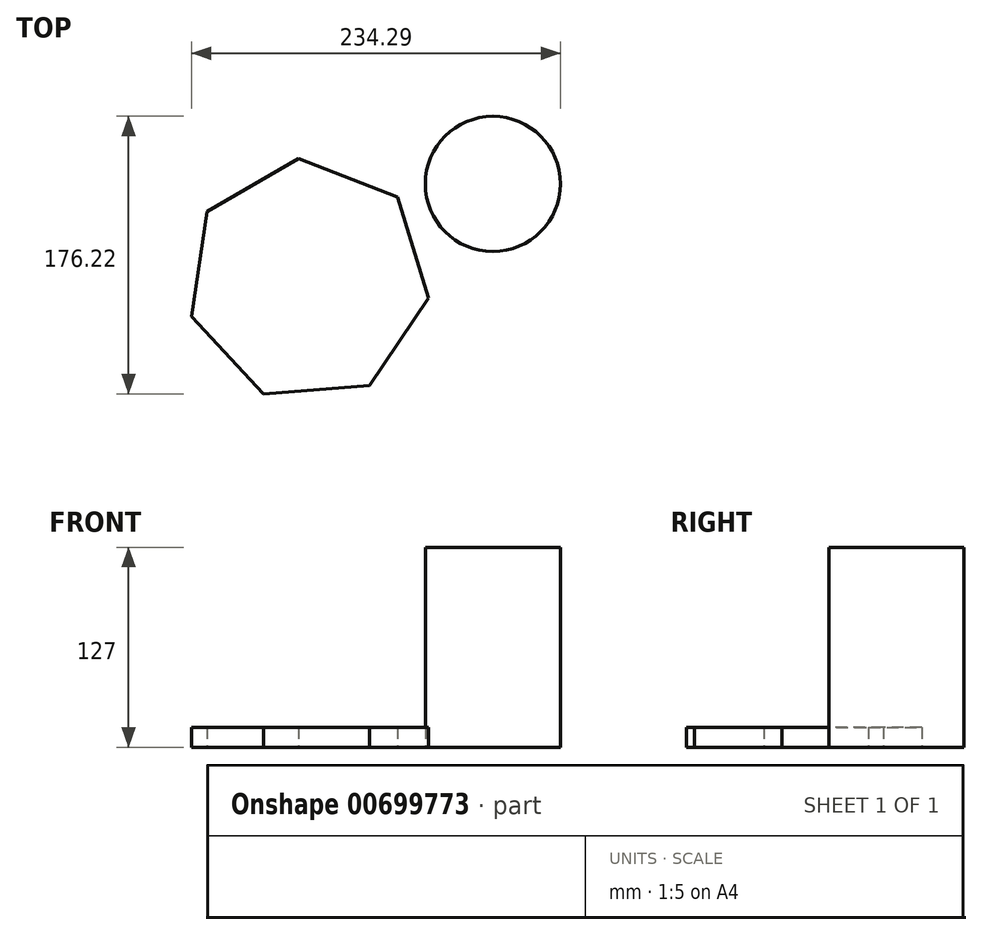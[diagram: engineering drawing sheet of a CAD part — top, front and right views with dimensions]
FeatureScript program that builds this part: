
annotation { "Feature Type Name" : "Feature", "Feature Type Description" : "" }
export const myFeature = defineFeature(function(context is Context, id is Id, definition is map)
    precondition{}
    {
        {
            var Q0;
            Q0=qCreatedBy(makeId("Top.planeOp"),FACE);
            var sketch = newSketch(context, id + "F0", { "sketchPlane" : qUnion([Q0])});
            skCircle(sketch, "E0.cCircle", {"center": v(-129.2, -13.24) * mm, "radius": 69.81 * mm, "construction": true});
            skLineSegment(sketch, "E0.0", {"start": v(-72.52, 39.59) * mm, "end": v(-52.56, -24.62) * mm});
            skLineSegment(sketch, "E0.1", {"start": v(-52.56, -24.62) * mm, "end": v(-90.31, -80.26) * mm});
            skLineSegment(sketch, "E0.2", {"start": v(-90.31, -80.26) * mm, "end": v(-157.35, -85.43) * mm});
            skLineSegment(sketch, "E0.3", {"start": v(-157.35, -85.43) * mm, "end": v(-203.2, -36.24) * mm});
            skLineSegment(sketch, "E0.4", {"start": v(-203.2, -36.24) * mm, "end": v(-193.32, 30.27) * mm});
            skLineSegment(sketch, "E0.5", {"start": v(-193.32, 30.27) * mm, "end": v(-135.16, 64.02) * mm});
            skLineSegment(sketch, "E0.6", {"start": v(-135.16, 64.02) * mm, "end": v(-72.52, 39.59) * mm});
            skPoint(sketch, "E0.0.midPoint", {"position": v(-62.54, 7.48) * mm});
            skSolve(sketch);
        }
        {
            var Q0;
            Q0=makeQuery(id+"F0.imprint","IMPRINT",FACE,{"disambiguationData":[TD([[makeQuery(id+"F0.imprint","IMPRINT",EDGE,{"derivedFrom":sQuery(id+"F0.wireOp",EDGE,"E0.0")}),-1.0]])]});
            var sketch = newSketch(context, id + "F1", { "sketchPlane" : qUnion([Q0])});
            skSolve(sketch);
        }
        {
            var Q0;
            Q0 = qSketchRegion(id + "F1", true);
            var Q1;
            Q1 = qSketchRegion(id + "F0", true);
            extrude(context, id + "F2", {"entities" : qUnion([Q0, Q1]), "depth" : 12.7 * mm, "offsetDistance" : 25.4 * mm});
        }
        {
            var Q0;
            Q0=qCreatedBy(makeId("Top.planeOp"),FACE);
            var sketch = newSketch(context, id + "F3", { "sketchPlane" : qUnion([Q0])});
            skCircle(sketch, "E1", {"center": v(-11.84, 47.86) * mm, "radius": 42.93 * mm});
            skSolve(sketch);
        }
        {
            var Q0;
            Q0=makeQuery(id+"F3.imprint","IMPRINT",FACE,{"disambiguationData":[TD([[makeQuery(id+"F3.imprint","IMPRINT",EDGE,{"derivedFrom":sQuery(id+"F3.wireOp",EDGE,"E1")}),1.0]])]});
            extrude(context, id + "F4", {"entities" : qUnion([Q0]), "depth" : 127 * mm, "offsetDistance" : 25.4 * mm});
        }
    });
